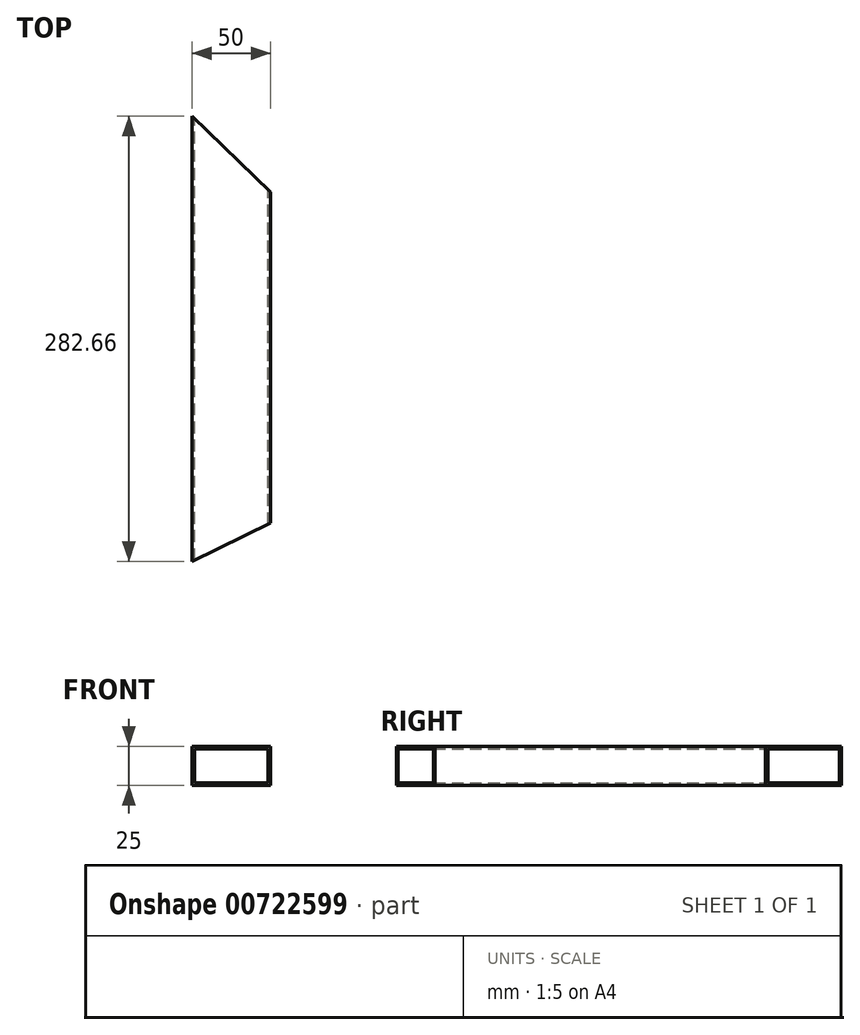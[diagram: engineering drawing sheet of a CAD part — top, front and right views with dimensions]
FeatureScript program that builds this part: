
annotation { "Feature Type Name" : "Feature", "Feature Type Description" : "" }
export const myFeature = defineFeature(function(context is Context, id is Id, definition is map)
    precondition{}
    {
        {
            var Q0;
            Q0=qCreatedBy(makeId("Front.planeOp"),FACE);
            var sketch = newSketch(context, id + "F0", { "sketchPlane" : qUnion([Q0])});
            skLineSegment(sketch, "E0.bottom", {"start": v(-25, -12.5) * mm, "end": v(25, -12.5) * mm});
            skLineSegment(sketch, "E0.top", {"start": v(-25, 12.5) * mm, "end": v(25, 12.5) * mm});
            skLineSegment(sketch, "E0.left", {"start": v(-25, -12.5) * mm, "end": v(-25, 12.5) * mm});
            skLineSegment(sketch, "E0.right", {"start": v(25, -12.5) * mm, "end": v(25, 12.5) * mm});
            skPoint(sketch, "E0.middle", {"position": v(0, 0) * mm});
            skLineSegment(sketch, "E1.bottom", {"start": v(-23.41, -10.91) * mm, "end": v(23.41, -10.91) * mm});
            skLineSegment(sketch, "E1.top", {"start": v(-23.41, 10.91) * mm, "end": v(23.41, 10.91) * mm});
            skLineSegment(sketch, "E1.left", {"start": v(-23.41, -10.91) * mm, "end": v(-23.41, 10.91) * mm});
            skLineSegment(sketch, "E1.right", {"start": v(23.41, -10.91) * mm, "end": v(23.41, 10.92) * mm});
            skSolve(sketch);
        }
        {
            var Q0;
            Q0=makeQuery(id+"F0.imprint","IMPRINT",FACE,{"disambiguationData":[TD([[makeQuery(id+"F0.imprint","IMPRINT",EDGE,{"derivedFrom":sQuery(id+"F0.wireOp",EDGE,"E0.bottom")}),1.0]])]});
            extrude(context, id + "F1", {"entities" : qUnion([Q0]), "endBound" : BoundingType.SYMMETRIC, "depth" : 283.82 * mm, "offsetDistance" : 25 * mm});
        }
        {
            var Q0;
            Q0=makeQuery(id+"F1.opExtrude","CAP_EDGE",EDGE,{"disambiguationData":[OSD([sQuery(id+"F0.wireOp",EDGE,"E0.right")])],"isStart":false});
            chamfer(context, id + "F2", {"entities" : qUnion([Q0]), "chamferType" : ChamferType.TWO_OFFSETS, "width1" : 50.8 * mm, "oppositeDirection" : false, "width2" : 24.77 * mm, "tangentPropagation" : true});
        }
        {
            var Q0;
            Q0=makeQuery(id+"F1.opExtrude","CAP_EDGE",EDGE,{"disambiguationData":[OSD([sQuery(id+"F0.wireOp",EDGE,"E0.right")])],"isStart":true});
            chamfer(context, id + "F3", {"entities" : qUnion([Q0]), "chamferType" : ChamferType.TWO_OFFSETS, "width1" : 50.8 * mm, "oppositeDirection" : true, "width2" : 49.05 * mm, "tangentPropagation" : true});
        }
    });
